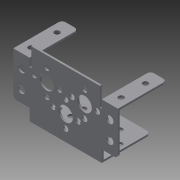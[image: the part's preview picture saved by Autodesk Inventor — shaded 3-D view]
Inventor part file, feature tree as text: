
AUTODESK INVENTOR PART (.ipt)
format: ipt  version: 2015 (Build 190159000, 159)  size: 254,976 bytes
history: native  units: mm
features: extrude x5, sketch x5, fillet x1
ambient origin geometry x8: Origin, YZ Plane, XZ Plane, XY Plane, X Axis, Y Axis, Z Axis, Center Point
bodies: Solid1 (feature_tree)
feature tree (11):
  extrude  "Extrusion1"  Depth=40.0mm TaperAngle=360.0deg
  extrude  "Extrusion2"  Depth=29.0mm
  fillet  "Fillet1"  Radius=10.5mm
  extrude  "Extrusion3"  Depth=1.0mm
  extrude  "Extrusion4"  Depth=1.0mm
  extrude  "Extrusion5"  Depth=4.0mm
  sketch  "Sketch2"  dims[d10=40.0mm d12=360.0deg d18=40.0mm d19=360.0deg d22=10.0mm]
  sketch  "Sketch3"  dims[d23=29.0mm d24=29.0mm d25=10.5mm]
  sketch  "Sketch4"  dims[d26=21.0mm d32=1.0mm]
  sketch  "Sketch5"  dims[d33=3.5mm d34=1.0mm]
  sketch  "Sketch6"  dims[d37=4.0mm d38=4.0mm d41=2.0mm d42=1.0mm d43=0.0mm d44=1.0mm d45=1.0mm d46=1.0mm d47=26.0mm d48=0.0mm d49=2.0mm d52=3.0mm d53=40.0mm d55=360.0deg d58=3.0mm d59=3.0mm d60=40.0mm d62=360.0deg d64=26.0mm d65=0.0mm d66=3.0mm d67=26.0mm d68=0.0mm d69=14.5mm d70=7.25mm d71=3.0mm d72=3.0mm d73=3.0mm d74=26.0mm d75=0.0mm]
